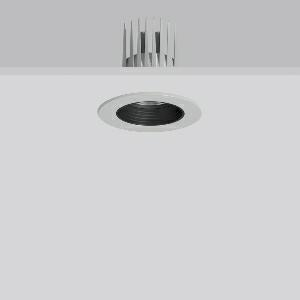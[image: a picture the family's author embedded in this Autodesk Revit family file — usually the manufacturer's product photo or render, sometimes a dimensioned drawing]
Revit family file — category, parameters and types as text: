
# Revit family: heledon_mini_e_901752_004_3_76_3585
name_source: partatom
category: Lighting Fixtures
units: mm (PartAtom-declared; Revit-internal decimal feet)

## family parameters
Cut with Voids When Loaded = No
Host = Face
Light Source = No
Part Type = Normal
Room Calculation Point = No
Round Connector Dimension = Use Diameter
Shared = No

## types (1)
- HELEDON mini E (1 x LED Modul 935, 3050 lm, 3500)
    Apparent Load = 29 VA
    Approval mark = CE
    CIE Flux Codes = 96 100 100 100 100
    Color Rendering = 92
    Color Temperature = 3500
    Default Elevation = 1800 mm
    Description = Series: HELEDON mini
Round recessed downlight. Housing: die-cast aluminium, powder-coated. Black plastic ring and recessed LED to prevent glare from the side. Optical assembly with lens made of plastic (polycarbonate) for the best homogeneous light distribution - can be changed without tools. Best colour rendering index Ra>90. Suitable for Recessed ceiling mounting. Installation without tools thanks to spring fastening system. Including separate LED converter with connecting cable 600 mm.High quality converter without flickering and stroboscopic effect. Through-wiring box (5 pole) available as accessory. The following accessories can be mounted without use of tools: interchangeable lenses, decorative glasses, honeycomb louvre, clear and frosted diffusers, white interchangeable plastic ring. 
Colour: silver
Diameter: 124 mm
Height: 3 mm
Cut-out diameter: 114 mm
Recess height: 170 mm
Luminaire: recess height: 120 mm
Lamp: LED
Socket: without socket
Colour temperature: 3500K
Colour rendering index (CRI): 92
System power: 29 W
Rated luminous flux: 3050 lm
Luminous efficiency: 105 lm/W
Control gear: Converter, dimmable, DALI
Protection class: II
Type of protection: IP 20
    Height = 0 mm  [stored 0 ft]
    Lamp = 1 x LED Modul 935
    Lamp Light Flux = 3050 lm
    Lamp count = 1
    Length = 124 mm  [stored 0.406824 ft]
    Lifetime = 50000 h
    Luminous efficacy = 105 lm/W
    Manufacturer = RZB
    ModVariant = No
    Model = 901752.004.3.76
    Mounting Place = Ceiling
    Mounting Type = Recessed
    Number of Poles = 1
    OnlyDefault = Yes
    Power Factor = 1
    Product Name = HELEDON mini E
    Product group = Recessed downlights
    ProductGroupID = 402
    Protection Class = Protection class II
    Protection Degree = IP 20
    RLX_Detail_Level = 1
    RLX_Emergency_Light_Flux = 0 lm
    RLX_Emergency_Type = 0
    RLX_Emergency_Type_DB = No
    RlxData = <blob elided: 125009 chars, md5=dc3267bf>
    Socket = socket
    Standby Power = 0 W
    System Light Flux = 3050 lm
    System Power = 29 W
    Type Comments = Product without accessories
    Type Image = 901656.004.jpg
    URL = http://relux.com
    VarID = ---
    Voltage = 230 V
    Voltage Range = 220-240 V
    Weight = 0.00 kg
    Width = 0 mm  [stored 0 ft]

note: [stored X ft] marks values corroborated as IEEE doubles in the binary element streams (Revit-internal decimal feet)

## geometry (parser evidence)
native form markers: Blend x4, Sweep x12
no freeform markers — native parametric forms only
